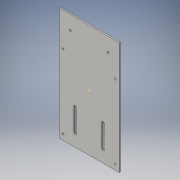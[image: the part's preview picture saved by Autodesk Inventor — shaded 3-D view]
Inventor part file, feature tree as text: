
AUTODESK INVENTOR PART (.ipt)
format: ipt  version: 2016 (Build 200138000, 138)  size: 143,360 bytes
history: native  units: in
note: dims shown in document units (in); Inventor stores cm internally (conversion verified against a paired STEP export)
features: sketch x4, extrude x2, hole x2, other x1
ambient origin geometry x8: Origin, YZ Plane, XZ Plane, XY Plane, X Axis, Y Axis, Z Axis, Center Point
bodies: Solid1 (feature_tree)
feature tree (9):
  extrude  "Extrusion1"  Depth=10.135in
  hole  "Hole1"  [1 undecoded]
  extrude  "Extrusion2"  Depth=3.0in
  hole  "Hole2"  [1 undecoded]
  other  "battery_buzzer"
  sketch  "Sketch1"  dims[d0=5.4in d1=10.135in]
  sketch  "Sketch2"  dims[d2=0.125in d3=0.0in d4=0.35in]
  sketch  "Sketch4"  dims[d5=3.0in d6=3.0in]
  sketch  "Sketch5"  dims[d7=0.35in d8=0.165in d9=0.5in d10=0.35in d11=0.35in d12=0.5in d13=0.165in d14=0.165in d15=0.75in d16=0.375in d17=0.25in d18=0.5635in d19=1.0in d20=0.8108in d21=0.165in d22=0.165in d23=0.27in d24=0.27in d25=1.315in d26=2.0in d27=1.315in d28=1.135in d29=1.135in d30=1.135in d31=1.135in d32=2.0in d33=2.0in d34=2.0in d35=0.125in d36=0.0in d37=1.25in d38=3.412in d39=1.25in d40=0.994in d41=0.176in d42=0.75in d43=0.375in d44=0.25in d45=0.5635in d46=1.0in d47=0.8108in]
note: 2 required parameter values undecoded (feature->parameter linkage not recoverable at this tier; creation-order binding heuristic only, values carry confidence <= 0.55)
